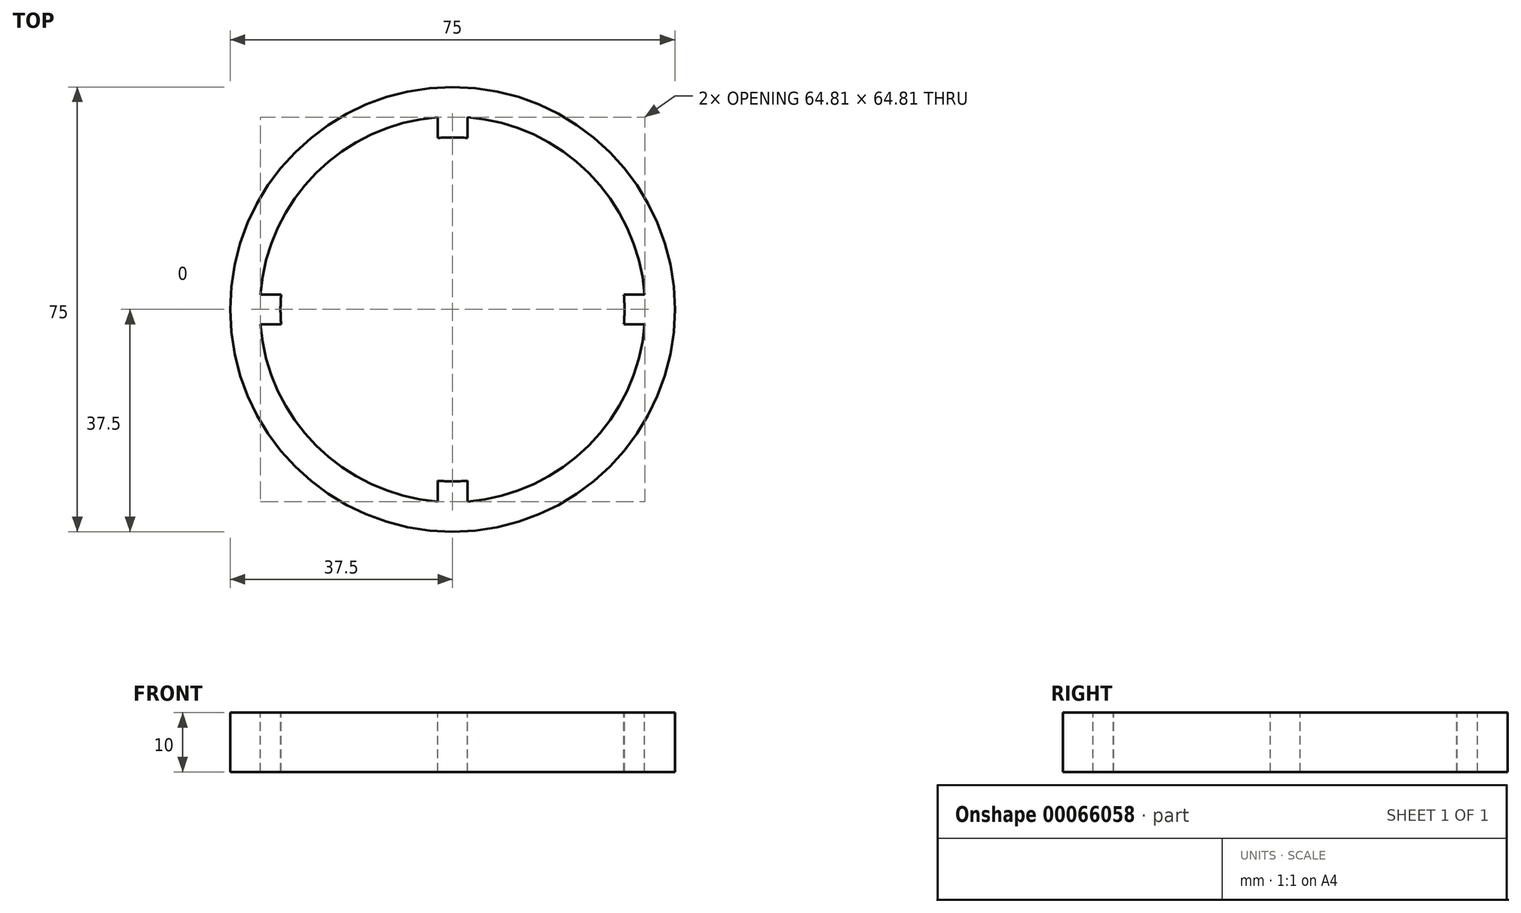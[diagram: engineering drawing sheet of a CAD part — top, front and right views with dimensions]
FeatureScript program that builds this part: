
annotation { "Feature Type Name" : "Feature", "Feature Type Description" : "" }
export const myFeature = defineFeature(function(context is Context, id is Id, definition is map)
    precondition{}
    {
        {
            var Q0;
            Q0=qCreatedBy(makeId("Top.planeOp"),FACE);
            var sketch = newSketch(context, id + "F0", { "sketchPlane" : qUnion([Q0])});
            skCircle(sketch, "E0", {"center": v(0, 0) * mm, "radius": 32.5 * mm});
            skCircle(sketch, "E1", {"center": v(0, 0) * mm, "radius": 37.5 * mm});
            skArc(sketch, "E2", {"start": v(-28.9, 2.5) * mm, "mid": v(-29, 0) * mm, "end": v(-28.9, -2.5) * mm});
            skLineSegment(sketch, "E3.trimOffspring", {"start": v(-32.4, 2.5) * mm, "end": v(-28.9, 2.5) * mm});
            skLineSegment(sketch, "E4.trimOffspring", {"start": v(-32.4, -2.5) * mm, "end": v(-28.9, -2.5) * mm});
            skLineSegment(sketch, "E5.trimOffspring", {"start": v(28.9, 2.5) * mm, "end": v(32.4, 2.5) * mm});
            skLineSegment(sketch, "E6.trimOffspring", {"start": v(28.9, -2.5) * mm, "end": v(32.4, -2.5) * mm});
            skLineSegment(sketch, "E7.trimOffspring", {"start": v(-2.5, 28.9) * mm, "end": v(-2.5, 32.4) * mm});
            skLineSegment(sketch, "E8.trimOffspring", {"start": v(2.5, 28.9) * mm, "end": v(2.5, 32.4) * mm});
            skLineSegment(sketch, "E9.trimOffspring", {"start": v(2.5, -32.4) * mm, "end": v(2.5, -28.9) * mm});
            skLineSegment(sketch, "E10.trimOffspring", {"start": v(-2.5, -32.4) * mm, "end": v(-2.5, -28.9) * mm});
            skArc(sketch, "E11.trimOffspring", {"start": v(2.5, 28.9) * mm, "mid": v(0, 29) * mm, "end": v(-2.5, 28.9) * mm});
            skArc(sketch, "E12.trimOffspring", {"start": v(28.9, -2.5) * mm, "mid": v(29, 0) * mm, "end": v(28.9, 2.5) * mm});
            skArc(sketch, "E13.trimOffspring", {"start": v(-2.5, -28.9) * mm, "mid": v(0, -29) * mm, "end": v(2.5, -28.9) * mm});
            skSolve(sketch);
        }
        {
            var Q0;
            Q0=makeQuery(id+"F0.imprint","IMPRINT",FACE,{"disambiguationData":[TD([[makeQuery(id+"F0.imprint","IMPRINT",EDGE,{"derivedFrom":sQuery(id+"F0.wireOp",EDGE,"E1")}),1.0]])]});
            var Q1;
            {var subQ1=sQuery(id+"F0.wireOp",EDGE,"E7.trimOffspring");Q1=makeQuery(id+"F0.imprint","IMPRINT",FACE,{"disambiguationData":[TD([[makeQuery(id+"F0.imprint","IMPRINT",EDGE,{"derivedFrom":subQ1}),-1.0]])]});}
            var Q2;
            {var subQ1=sQuery(id+"F0.wireOp",EDGE,"E5.trimOffspring");Q2=makeQuery(id+"F0.imprint","IMPRINT",FACE,{"disambiguationData":[TD([[makeQuery(id+"F0.imprint","IMPRINT",EDGE,{"derivedFrom":subQ1}),-1.0]])]});}
            var Q3;
            {var subQ1=sQuery(id+"F0.wireOp",EDGE,"E9.trimOffspring");Q3=makeQuery(id+"F0.imprint","IMPRINT",FACE,{"disambiguationData":[TD([[makeQuery(id+"F0.imprint","IMPRINT",EDGE,{"derivedFrom":subQ1}),1.0]])]});}
            var Q4;
            Q4=makeQuery(id+"F0.imprint","IMPRINT",FACE,{"disambiguationData":[TD([[makeQuery(id+"F0.imprint","IMPRINT",EDGE,{"derivedFrom":sQuery(id+"F0.wireOp",EDGE,"E2")}),-1.0]])]});
            extrude(context, id + "F1", {"entities" : qUnion([Q0, Q1, Q2, Q3, Q4]), "oppositeDirection" : true, "depth" : 10 * mm});
        }
    });
